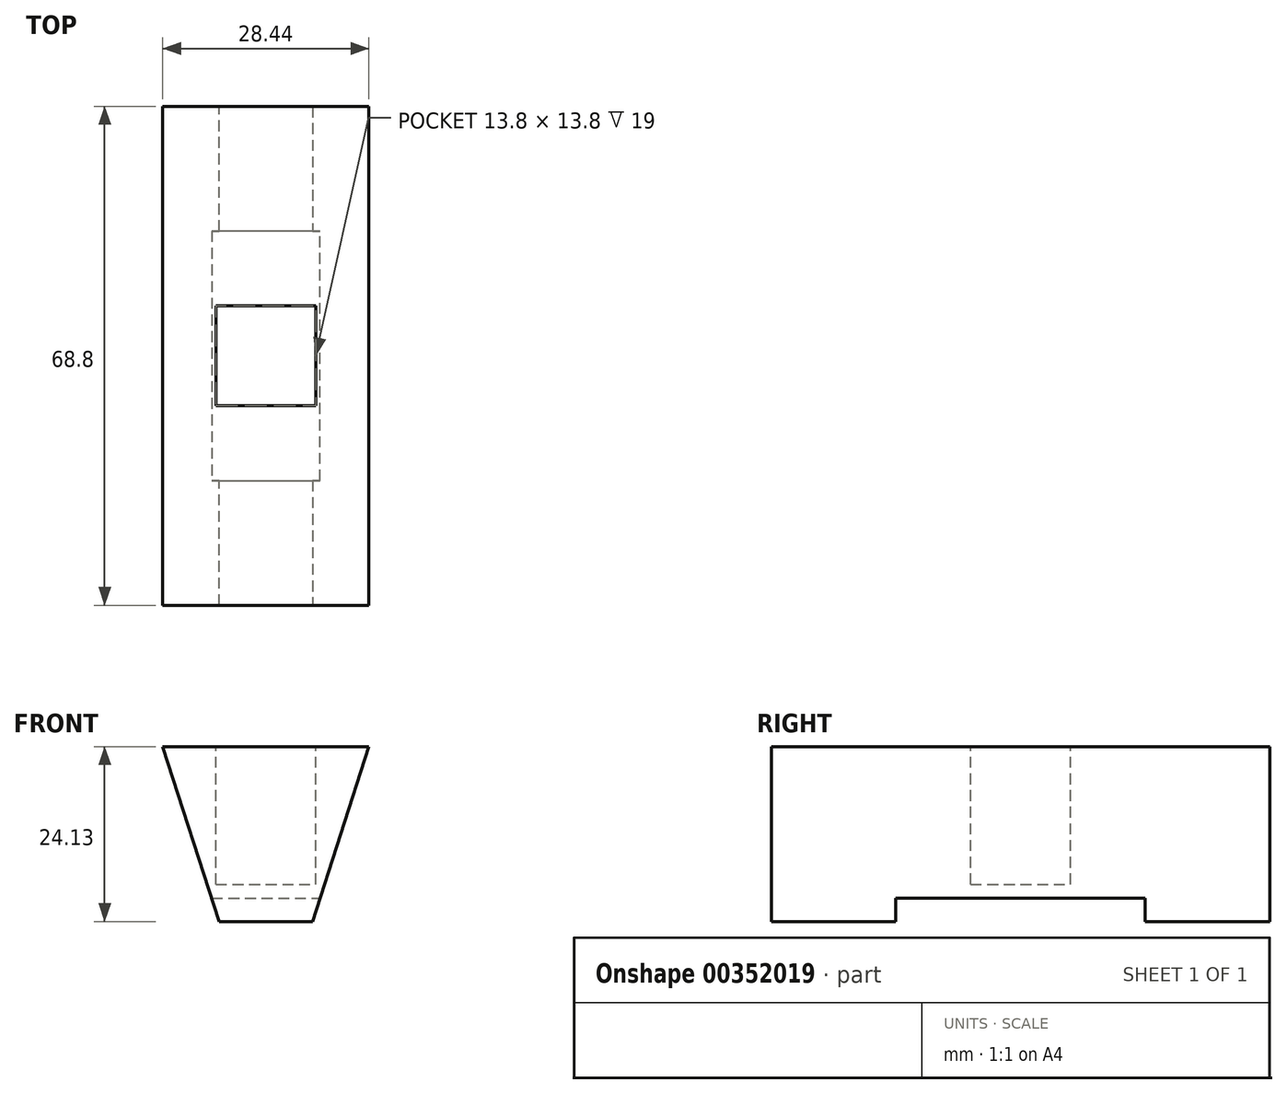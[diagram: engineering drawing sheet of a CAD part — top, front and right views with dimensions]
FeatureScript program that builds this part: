
annotation { "Feature Type Name" : "Feature", "Feature Type Description" : "" }
export const myFeature = defineFeature(function(context is Context, id is Id, definition is map)
    precondition{}
    {
        {
            var Q0;
            Q0=qCreatedBy(makeId("Top.planeOp"),FACE);
            cPlane(context, id + "F0", {"entities" : qUnion([Q0]), "cplaneType" : CPlaneType.OFFSET, "offset" : 36.12 * mm, "width" : 150 * mm, "height" : 150 * mm});
        }
        {
            var Q0;
            Q0=qCreatedBy(id+"F0.planeOp",FACE);
            var sketch = newSketch(context, id + "F1", { "sketchPlane" : qUnion([Q0])});
            skLineSegment(sketch, "E0", {"start": v(-18.1, 0) * mm, "end": v(-18.1, -68.8) * mm});
            skLineSegment(sketch, "E1", {"start": v(-18.1, -68.8) * mm, "end": v(18.1, -68.8) * mm});
            skLineSegment(sketch, "E2", {"start": v(18.1, -68.8) * mm, "end": v(18.1, 0) * mm});
            skLineSegment(sketch, "E3", {"start": v(-18.1, 0) * mm, "end": v(18.1, 0) * mm});
            skSolve(sketch);
        }
        {
            var Q0;
            Q0=qCreatedBy(makeId("Top.planeOp"),FACE);
            var sketch = newSketch(context, id + "F2", { "sketchPlane" : qUnion([Q0])});
            skLineSegment(sketch, "E4", {"start": v(6.43, 0) * mm, "end": v(6.43, -68.8) * mm});
            skLineSegment(sketch, "E5", {"start": v(6.43, -68.8) * mm, "end": v(-6.43, -68.8) * mm});
            skLineSegment(sketch, "E6", {"start": v(-6.43, -68.8) * mm, "end": v(-6.43, 0) * mm});
            skLineSegment(sketch, "E7", {"start": v(-6.43, 0) * mm, "end": v(6.43, 0) * mm});
            skSolve(sketch);
        }
        {
            var Q0;
            Q0=makeQuery(id+"F1.imprint","IMPRINT",FACE,{"disambiguationData":[TD([[makeQuery(id+"F1.imprint","IMPRINT",EDGE,{"derivedFrom":sQuery(id+"F1.wireOp",EDGE,"E0")}),1.0]])]});
            var Q1;
            Q1=makeQuery(id+"F2.imprint","IMPRINT",FACE,{"disambiguationData":[TD([[makeQuery(id+"F2.imprint","IMPRINT",EDGE,{"derivedFrom":sQuery(id+"F2.wireOp",EDGE,"E4")}),-1.0]])]});
            loft(context, id + "F3", {"sheetProfilesArray" : [{ "sheetProfileEntities" : qUnion([Q0]) }, { "sheetProfileEntities" : qUnion([Q1]) }]});
        }
        {
            var Q0;
            Q0=makeQuery(id+"F3.opLoft","CAP_FACE",FACE,{"disambiguationData":[OSD([makeQuery(id+"F1.imprint","IMPRINT",FACE,{"disambiguationData":[TD([[makeQuery(id+"F1.imprint","IMPRINT",EDGE,{"derivedFrom":sQuery(id+"F1.wireOp",EDGE,"E0")}),1.0]])]})])],"isStart":true});
            extrude(context, id + "F4", {"entities" : qUnion([Q0]), "operationType" : NewBodyOperationType.REMOVE, "oppositeDirection" : true, "depth" : 12 * mm});
        }
        {
            var Q0;
            Q0=qCreatedBy(id+"F0.planeOp",FACE);
            var sketch = newSketch(context, id + "F5", { "sketchPlane" : qUnion([Q0])});
            skLineSegment(sketch, "E8", {"start": v(-6.9, -27.5) * mm, "end": v(6.9, -27.5) * mm});
            skLineSegment(sketch, "E9", {"start": v(6.9, -27.5) * mm, "end": v(6.9, -41.3) * mm});
            skLineSegment(sketch, "E10", {"start": v(6.9, -41.3) * mm, "end": v(-6.9, -41.3) * mm});
            skLineSegment(sketch, "E11", {"start": v(-6.9, -41.3) * mm, "end": v(-6.9, -27.5) * mm});
            skSolve(sketch);
        }
        {
            var Q0;
            Q0=makeQuery(id+"F5.imprint","IMPRINT",FACE,{"disambiguationData":[TD([[makeQuery(id+"F5.imprint","IMPRINT",EDGE,{"derivedFrom":sQuery(id+"F5.wireOp",EDGE,"E8")}),-1.0]])]});
            extrude(context, id + "F6", {"entities" : qUnion([Q0]), "operationType" : NewBodyOperationType.REMOVE, "oppositeDirection" : true, "depth" : 31 * mm});
        }
        {
            var Q0;
            Q0=qCreatedBy(makeId("Top.planeOp"),FACE);
            var sketch = newSketch(context, id + "F7", { "sketchPlane" : qUnion([Q0])});
            skLineSegment(sketch, "E12", {"start": v(-10, -51.6) * mm, "end": v(10, -51.6) * mm});
            skLineSegment(sketch, "E13", {"start": v(10, -51.6) * mm, "end": v(10, -17.2) * mm});
            skLineSegment(sketch, "E14", {"start": v(10, -17.2) * mm, "end": v(-10, -17.2) * mm});
            skLineSegment(sketch, "E15", {"start": v(-10, -17.2) * mm, "end": v(-10, -51.6) * mm});
            skSolve(sketch);
        }
        {
            var Q0;
            Q0 = qSketchRegion(id + "F7", true);
            extrude(context, id + "F8", {"entities" : qUnion([Q0]), "operationType" : NewBodyOperationType.REMOVE, "depth" : 3.2 * mm});
        }
    });
